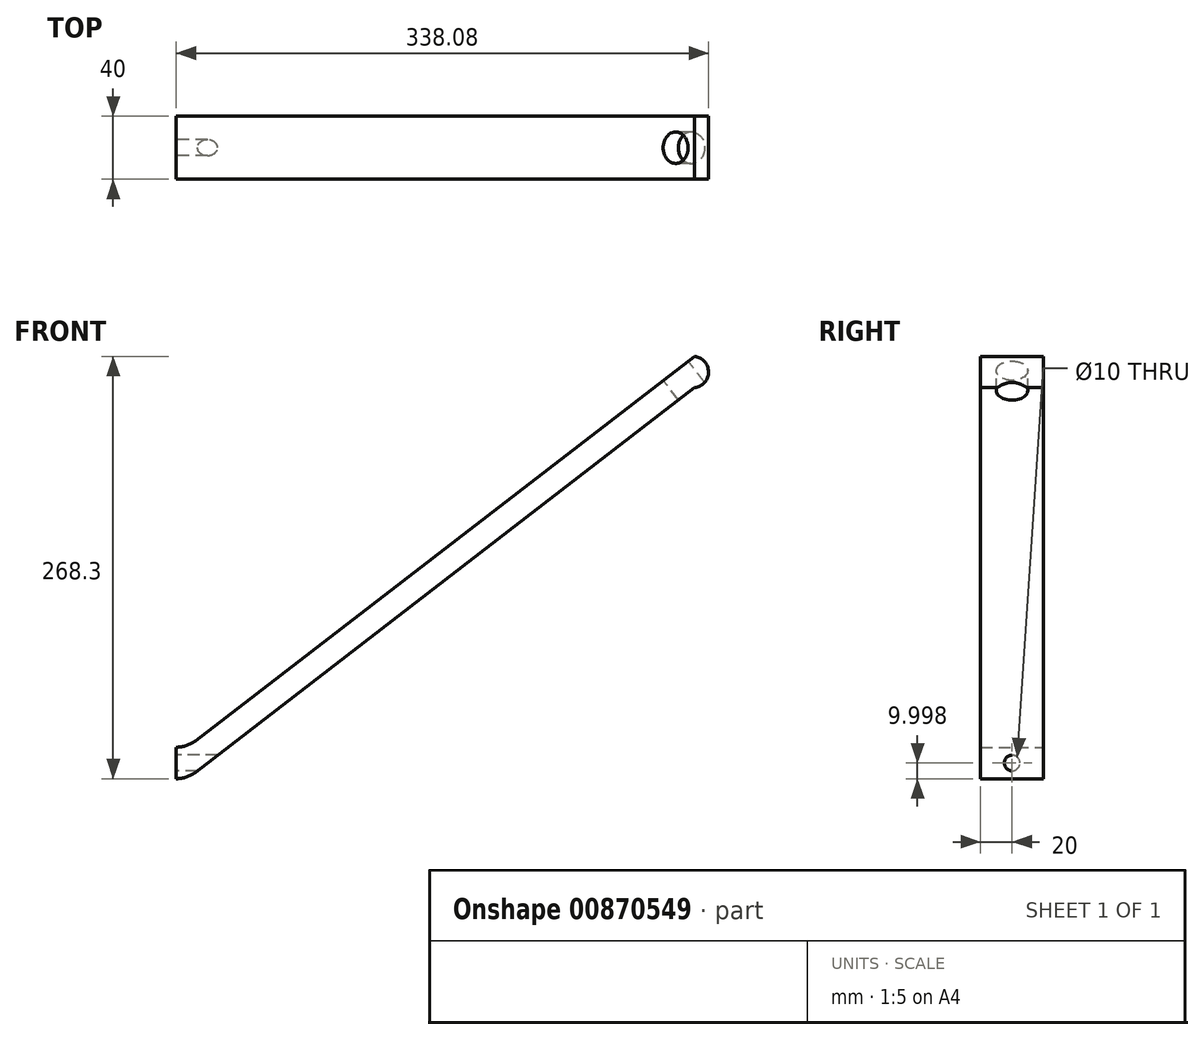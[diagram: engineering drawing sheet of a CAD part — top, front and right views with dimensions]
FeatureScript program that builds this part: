
annotation { "Feature Type Name" : "Feature", "Feature Type Description" : "" }
export const myFeature = defineFeature(function(context is Context, id is Id, definition is map)
    precondition{}
    {
        {
            var Q0;
            Q0=qCreatedBy(makeId("Front.planeOp"),FACE);
            var sketch = newSketch(context, id + "F0", { "sketchPlane" : qUnion([Q0])});
            skLineSegment(sketch, "E0.bottom", {"start": v(-150.86, -10.11) * mm, "end": v(-150.86, -10.11) * mm});
            skLineSegment(sketch, "E0.top", {"start": v(-150.86, -30.11) * mm, "end": v(-150.86, -30.11) * mm});
            skLineSegment(sketch, "E0.left", {"start": v(-150.86, -10.11) * mm, "end": v(-150.86, -30.11) * mm});
            skLineSegment(sketch, "E0.right", {"start": v(-144.05, -10.11) * mm, "end": v(-144.05, -30.11) * mm});
            skLineSegment(sketch, "E1", {"start": v(-138.65, -25.95) * mm, "end": v(178.34, 218.3) * mm});
            skLineSegment(sketch, "E2", {"start": v(178.2, 238.19) * mm, "end": v(-138.65, -5.95) * mm});
            skArc(sketch, "E3", {"start": v(178.34, 218.3) * mm, "mid": v(187.22, 228.3) * mm, "end": v(178.2, 238.19) * mm});
            skPoint(sketch, "E4.visualSharp", {"position": v(-144.05, -10.11) * mm});
            skArc(sketch, "E4.filletArc", {"start": v(-150.86, -10.11) * mm, "mid": v(-144.41, -9.04) * mm, "end": v(-138.65, -5.95) * mm});
            skPoint(sketch, "E5.visualSharp", {"position": v(-144.05, -30.11) * mm});
            skArc(sketch, "E5.filletArc", {"start": v(-150.86, -30.11) * mm, "mid": v(-144.41, -29.04) * mm, "end": v(-138.65, -25.95) * mm});
            skSolve(sketch);
        }
        {
            var Q0;
            {var subQ1=sQuery(id+"F0.wireOp",EDGE,"E0.left");Q0=makeQuery(id+"F0.imprint","IMPRINT",FACE,{"disambiguationData":[TD([[makeQuery(id+"F0.imprint","IMPRINT",EDGE,{"derivedFrom":subQ1}),1.0]])]});}
            extrude(context, id + "F1", {"entities" : qUnion([Q0]), "depth" : 40 * mm, "offsetDistance" : 25 * mm});
        }
        {
            var Q0;
            Q0=makeQuery(id+"F1.opExtrude","SWEPT_FACE",FACE,{"disambiguationData":[OSD([sQuery(id+"F0.wireOp",EDGE,"E0.left")])]});
            var sketch = newSketch(context, id + "F2", { "sketchPlane" : qUnion([Q0])});
            skPoint(sketch, "E6", {"position": v(20, -20.11) * mm});
            skSolve(sketch);
        }
        {
            var Q0;
            Q0=sQuery(id+"F2.wireOp",VERTEX,"E6");
            var Q1;
            Q1=makeQuery(id+"F1.opExtrude","SWEPT_BODY",BODY,{"disambiguationData":[OSD([sQuery(id+"F0.wireOp",EDGE,"E0.left"),sQuery(id+"F0.wireOp",EDGE,"E1"),sQuery(id+"F0.wireOp",EDGE,"E2"),sQuery(id+"F0.wireOp",EDGE,"E3"),sQuery(id+"F0.wireOp",EDGE,"E4.filletArc"),sQuery(id+"F0.wireOp",EDGE,"E5.filletArc")])]});
            hole(context, id + "F3", {"style" : HoleStyle.SIMPLE, "endStyle" : HoleEndStyle.THROUGH, "holeDiameter" : 10 * mm, "majorDiameter" : 5 * mm, "isTappedThrough" : true, "tappedDepth" : 12 * mm, "tapClearance" : 3, "locations" : qUnion([Q0]), "scope" : qUnion([Q1])});
        }
        {
            var Q0;
            Q0=makeQuery(id+"F1.opExtrude","SWEPT_FACE",FACE,{"disambiguationData":[OSD([sQuery(id+"F0.wireOp",EDGE,"E2")])]});
            var sketch = newSketch(context, id + "F4", { "sketchPlane" : qUnion([Q0])});
            skPoint(sketch, "E7", {"position": v(271.54, -20) * mm});
            skSolve(sketch);
        }
        {
            var Q0;
            Q0=sQuery(id+"F4.wireOp",VERTEX,"E7");
            var Q1;
            Q1=makeQuery(id+"F1.opExtrude","SWEPT_BODY",BODY,{"disambiguationData":[OSD([sQuery(id+"F0.wireOp",EDGE,"E0.left"),sQuery(id+"F0.wireOp",EDGE,"E1"),sQuery(id+"F0.wireOp",EDGE,"E2"),sQuery(id+"F0.wireOp",EDGE,"E3"),sQuery(id+"F0.wireOp",EDGE,"E4.filletArc"),sQuery(id+"F0.wireOp",EDGE,"E5.filletArc")])]});
            hole(context, id + "F5", {"style" : HoleStyle.SIMPLE, "endStyle" : HoleEndStyle.THROUGH, "holeDiameter" : 20 * mm, "majorDiameter" : 5 * mm, "isTappedThrough" : true, "tappedDepth" : 12 * mm, "tapClearance" : 3, "locations" : qUnion([Q0]), "scope" : qUnion([Q1])});
        }
    });
